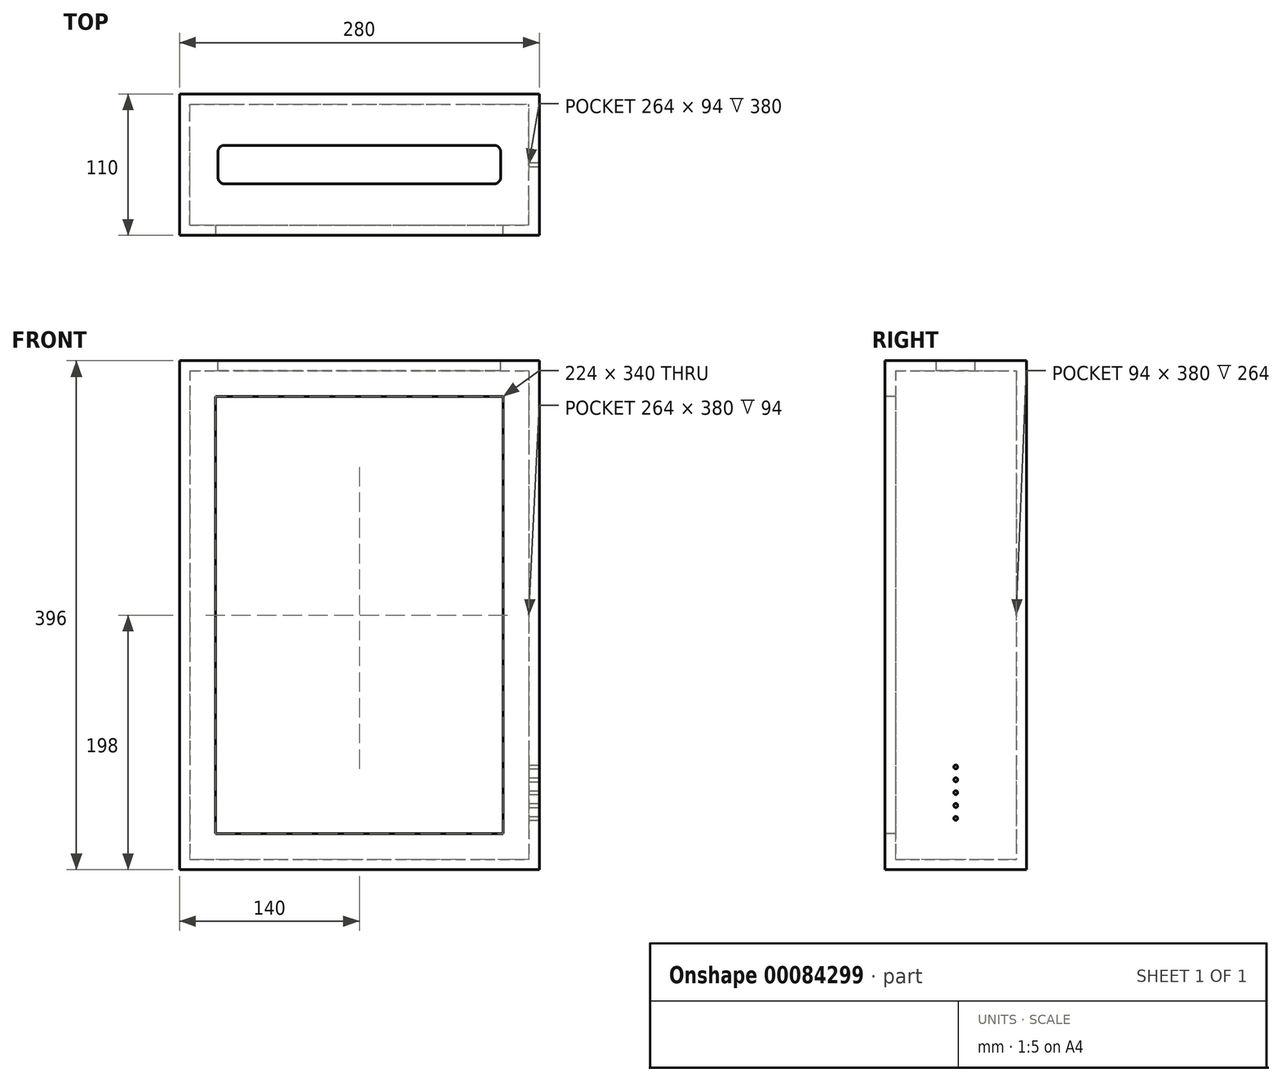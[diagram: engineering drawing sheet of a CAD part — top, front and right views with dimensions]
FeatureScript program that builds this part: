
annotation { "Feature Type Name" : "Feature", "Feature Type Description" : "" }
export const myFeature = defineFeature(function(context is Context, id is Id, definition is map)
    precondition{}
    {
        {
            var Q0;
            Q0=qCreatedBy(makeId("Top.planeOp"),FACE);
            var sketch = newSketch(context, id + "F0", { "sketchPlane" : qUnion([Q0])});
            skLineSegment(sketch, "E0.bottom", {"start": v(-140, 55) * mm, "end": v(140, 55) * mm});
            skLineSegment(sketch, "E0.top", {"start": v(-140, -55) * mm, "end": v(140, -55) * mm});
            skLineSegment(sketch, "E0.left", {"start": v(-140, 55) * mm, "end": v(-140, -55) * mm});
            skLineSegment(sketch, "E0.right", {"start": v(140, 55) * mm, "end": v(140, -55) * mm});
            skPoint(sketch, "E0.middle", {"position": v(0, 0) * mm});
            skSolve(sketch);
        }
        {
            var Q0;
            Q0=makeQuery(id+"F0.imprint","IMPRINT",FACE,{"disambiguationData":[TD([[makeQuery(id+"F0.imprint","IMPRINT",EDGE,{"derivedFrom":sQuery(id+"F0.wireOp",EDGE,"E0.bottom")}),-1.0]])]});
            extrude(context, id + "F1", {"entities" : qUnion([Q0]), "depth" : 8 * mm});
        }
        {
            var Q0;
            Q0=makeQuery(id+"F1.opExtrude","CAP_FACE",FACE,{"disambiguationData":[OSD([sQuery(id+"F0.wireOp",EDGE,"E0.bottom"),sQuery(id+"F0.wireOp",EDGE,"E0.top"),sQuery(id+"F0.wireOp",EDGE,"E0.left"),sQuery(id+"F0.wireOp",EDGE,"E0.right")])],"isStart":false});
            var sketch = newSketch(context, id + "F2", { "sketchPlane" : qUnion([Q0])});
            skLineSegment(sketch, "E1.bottom", {"start": v(-140, -55) * mm, "end": v(140, -55) * mm});
            skLineSegment(sketch, "E1.top", {"start": v(-140, 55) * mm, "end": v(140, 55) * mm});
            skLineSegment(sketch, "E1.left", {"start": v(-140, -55) * mm, "end": v(-140, 55) * mm});
            skLineSegment(sketch, "E1.right", {"start": v(140, -55) * mm, "end": v(140, 55) * mm});
            skPoint(sketch, "E1.middle", {"position": v(0, 0) * mm});
            skLineSegment(sketch, "E2.bottom", {"start": v(-132, -47) * mm, "end": v(132, -47) * mm});
            skLineSegment(sketch, "E2.top", {"start": v(-132, 47) * mm, "end": v(132, 47) * mm});
            skLineSegment(sketch, "E2.left", {"start": v(-132, -47) * mm, "end": v(-132, 47) * mm});
            skLineSegment(sketch, "E2.right", {"start": v(132, -47) * mm, "end": v(132, 47) * mm});
            skSolve(sketch);
        }
        {
            var Q0;
            Q0=makeQuery(id+"F2.imprint","IMPRINT",FACE,{"disambiguationData":[TD([[makeQuery(id+"F2.imprint","IMPRINT",EDGE,{"derivedFrom":sQuery(id+"F2.wireOp",EDGE,"E1.bottom")}),1.0]])]});
            extrude(context, id + "F3", {"entities" : qUnion([Q0]), "operationType" : NewBodyOperationType.ADD, "depth" : 20 * mm});
        }
        {
            var Q0;
            Q0=makeQuery(id+"F3.opExtrude","CAP_FACE",FACE,{"disambiguationData":[OSD([sQuery(id+"F2.wireOp",EDGE,"E1.bottom"),sQuery(id+"F2.wireOp",EDGE,"E1.top"),sQuery(id+"F2.wireOp",EDGE,"E1.left"),sQuery(id+"F2.wireOp",EDGE,"E1.right"),sQuery(id+"F2.wireOp",EDGE,"E2.bottom"),sQuery(id+"F2.wireOp",EDGE,"E2.top"),sQuery(id+"F2.wireOp",EDGE,"E2.left"),sQuery(id+"F2.wireOp",EDGE,"E2.right")])],"isStart":false});
            var sketch = newSketch(context, id + "F4", { "sketchPlane" : qUnion([Q0])});
            skLineSegment(sketch, "E3", {"start": v(-132, 47) * mm, "end": v(-132, -47) * mm});
            skLineSegment(sketch, "E4", {"start": v(-132, -47) * mm, "end": v(-112, -47) * mm});
            skLineSegment(sketch, "E5", {"start": v(-112, -47) * mm, "end": v(-112, -55) * mm});
            skLineSegment(sketch, "E6", {"start": v(-112, -55) * mm, "end": v(-140, -55) * mm});
            skLineSegment(sketch, "E7", {"start": v(-140, -55) * mm, "end": v(-140, 55) * mm});
            skLineSegment(sketch, "E8", {"start": v(-140, 55) * mm, "end": v(140, 55) * mm});
            skLineSegment(sketch, "E9", {"start": v(140, 55) * mm, "end": v(140, -55) * mm});
            skLineSegment(sketch, "E10", {"start": v(140, -55) * mm, "end": v(112, -55) * mm});
            skLineSegment(sketch, "E11", {"start": v(112, -55) * mm, "end": v(112, -47) * mm});
            skLineSegment(sketch, "E12", {"start": v(112, -47) * mm, "end": v(132, -47) * mm});
            skLineSegment(sketch, "E13", {"start": v(132, -47) * mm, "end": v(132, 47) * mm});
            skLineSegment(sketch, "E14", {"start": v(132, 47) * mm, "end": v(-132, 47) * mm});
            skSolve(sketch);
        }
        {
            var Q0;
            Q0=makeQuery(id+"F4.imprint","IMPRINT",FACE,{"disambiguationData":[TD([[makeQuery(id+"F4.imprint","IMPRINT",EDGE,{"derivedFrom":sQuery(id+"F4.wireOp",EDGE,"E3")}),1.0]])]});
            extrude(context, id + "F5", {"entities" : qUnion([Q0]), "operationType" : NewBodyOperationType.ADD, "depth" : 340 * mm});
        }
        {
            var Q0;
            Q0=makeQuery(id+"F5.opExtrude","CAP_FACE",FACE,{"disambiguationData":[OSD([sQuery(id+"F4.wireOp",EDGE,"E3"),sQuery(id+"F4.wireOp",EDGE,"E4"),sQuery(id+"F4.wireOp",EDGE,"E5"),sQuery(id+"F4.wireOp",EDGE,"E6"),sQuery(id+"F4.wireOp",EDGE,"E7"),sQuery(id+"F4.wireOp",EDGE,"E8"),sQuery(id+"F4.wireOp",EDGE,"E9"),sQuery(id+"F4.wireOp",EDGE,"E10"),sQuery(id+"F4.wireOp",EDGE,"E11"),sQuery(id+"F4.wireOp",EDGE,"E12"),sQuery(id+"F4.wireOp",EDGE,"E13"),sQuery(id+"F4.wireOp",EDGE,"E14")])],"isStart":false});
            var sketch = newSketch(context, id + "F6", { "sketchPlane" : qUnion([Q0])});
            skLineSegment(sketch, "E15.bottom", {"start": v(-132, -47) * mm, "end": v(132, -47) * mm});
            skLineSegment(sketch, "E15.top", {"start": v(-132, 47) * mm, "end": v(132, 47) * mm});
            skLineSegment(sketch, "E15.left", {"start": v(-132, -47) * mm, "end": v(-132, 47) * mm});
            skLineSegment(sketch, "E15.right", {"start": v(132, -47) * mm, "end": v(132, 47) * mm});
            skPoint(sketch, "E15.middle", {"position": v(0, 0) * mm});
            skLineSegment(sketch, "E16.bottom", {"start": v(-140, -55) * mm, "end": v(140, -55) * mm});
            skLineSegment(sketch, "E16.top", {"start": v(-140, 55) * mm, "end": v(140, 55) * mm});
            skLineSegment(sketch, "E16.left", {"start": v(-140, -55) * mm, "end": v(-140, 55) * mm});
            skLineSegment(sketch, "E16.right", {"start": v(140, -55) * mm, "end": v(140, 55) * mm});
            skSolve(sketch);
        }
        {
            var Q0;
            {var subQ1=makeQuery(id+"F5.opExtrude","CAP_EDGE",EDGE,{"disambiguationData":[OSD([sQuery(id+"F4.wireOp",EDGE,"E5")])],"isStart":false});Q0=makeQuery(id+"F6.imprint","IMPRINT",FACE,{"disambiguationData":[TD([[makeQuery(id+"F6.imprint","IMPRINT",EDGE,{"derivedFrom":subQ1}),1.0]])]});}
            var Q1;
            Q1=makeQuery(id+"F6.imprint","IMPRINT",FACE,{"disambiguationData":[TD([[makeQuery(id+"F6.imprint","IMPRINT",EDGE,{"derivedFrom":sQuery(id+"F6.wireOp",EDGE,"E15.top")}),1.0]])]});
            var Q2;
            Q2 = qSketchRegion(id + "F8", true);
            extrude(context, id + "F7", {"entities" : qUnion([Q0, Q1, Q2]), "operationType" : NewBodyOperationType.ADD, "depth" : 20 * mm, "offsetDistance" : 25 * mm});
        }
        {
            var Q0;
            Q0=makeQuery(id+"F7.opExtrude","CAP_FACE",FACE,{"disambiguationData":[OSD([sQuery(id+"F6.wireOp",EDGE,"E15.bottom"),sQuery(id+"F6.wireOp",EDGE,"E15.top"),sQuery(id+"F6.wireOp",EDGE,"E15.left"),sQuery(id+"F6.wireOp",EDGE,"E15.right"),sQuery(id+"F6.wireOp",EDGE,"E16.bottom"),sQuery(id+"F6.wireOp",EDGE,"E16.top"),sQuery(id+"F6.wireOp",EDGE,"E16.left"),sQuery(id+"F6.wireOp",EDGE,"E16.right")])],"isStart":false});
            var sketch = newSketch(context, id + "F8", { "sketchPlane" : qUnion([Q0])});
            skLineSegment(sketch, "E17.bottom", {"start": v(-140, -55) * mm, "end": v(140, -55) * mm});
            skLineSegment(sketch, "E17.top", {"start": v(-140, 55) * mm, "end": v(140, 55) * mm});
            skLineSegment(sketch, "E17.left", {"start": v(-140, -55) * mm, "end": v(-140, 55) * mm});
            skLineSegment(sketch, "E17.right", {"start": v(140, -55) * mm, "end": v(140, 55) * mm});
            skPoint(sketch, "E17.middle", {"position": v(0, 0) * mm});
            skSolve(sketch);
        }
        {
            var Q0;
            Q0=makeQuery(id+"F8.imprint","IMPRINT",FACE,{"disambiguationData":[TD([[makeQuery(id+"F8.imprint","IMPRINT",EDGE,{"derivedFrom":sQuery(id+"F8.wireOp",EDGE,"E17.bottom")}),1.0]])]});
            var Q1;
            Q1=makeQuery(id+"F8.imprint","IMPRINT",FACE,{"disambiguationData":[TD([[makeQuery(id+"F8.imprint","IMPRINT",EDGE,{"derivedFrom":makeQuery(id+"F7.opExtrude","CAP_EDGE",EDGE,{"disambiguationData":[OSD([sQuery(id+"F6.wireOp",EDGE,"E15.bottom")])],"isStart":false})}),1.0]])]});
            extrude(context, id + "F9", {"entities" : qUnion([Q0, Q1]), "operationType" : NewBodyOperationType.ADD, "depth" : 8 * mm, "offsetDistance" : 25 * mm});
        }
        {
            var Q0;
            Q0=makeQuery(id+"F9.boolean.opBoolean","MERGE",FACE,{"derivedFrom":[makeQuery(id+"F7.boolean.opBoolean","MERGE",FACE,{"derivedFrom":[makeQuery(id+"F5.boolean.opBoolean","MERGE",FACE,{"derivedFrom":[makeQuery(id+"F3.boolean.opBoolean","MERGE",FACE,{"derivedFrom":[makeQuery(id+"F1.opExtrude","SWEPT_FACE",FACE,{"disambiguationData":[OSD([sQuery(id+"F0.wireOp",EDGE,"E0.right")])]}),makeQuery(id+"F3.opExtrude","SWEPT_FACE",FACE,{"disambiguationData":[OSD([sQuery(id+"F2.wireOp",EDGE,"E1.right")])]})]}),makeQuery(id+"F5.opExtrude","SWEPT_FACE",FACE,{"disambiguationData":[OSD([sQuery(id+"F4.wireOp",EDGE,"E9")])]})]}),makeQuery(id+"F7.opExtrude","SWEPT_FACE",FACE,{"disambiguationData":[OSD([sQuery(id+"F6.wireOp",EDGE,"E16.right")])]})]}),makeQuery(id+"F9.opExtrude","SWEPT_FACE",FACE,{"disambiguationData":[OSD([sQuery(id+"F8.wireOp",EDGE,"E17.right")])]})]});
            var sketch = newSketch(context, id + "F10", { "sketchPlane" : qUnion([Q0])});
            skLineSegment(sketch, "E18", {"start": v(0, 0) * mm, "end": v(0, 396) * mm, "construction": true});
            skCircle(sketch, "E19", {"center": v(0, 40) * mm, "radius": 1.55 * mm});
            skCircle(sketch, "E20", {"center": v(0, 50) * mm, "radius": 1.55 * mm});
            skCircle(sketch, "E21", {"center": v(0, 60) * mm, "radius": 1.55 * mm});
            skCircle(sketch, "E22", {"center": v(0, 70) * mm, "radius": 1.55 * mm});
            skCircle(sketch, "E23", {"center": v(0, 80) * mm, "radius": 1.55 * mm});
            skSolve(sketch);
        }
        {
            var Q0;
            Q0=makeQuery(id+"F10.imprint","IMPRINT",FACE,{"disambiguationData":[TD([[makeQuery(id+"F10.imprint","IMPRINT",EDGE,{"derivedFrom":sQuery(id+"F10.wireOp",EDGE,"E23")}),1.0]])]});
            var Q1;
            Q1=makeQuery(id+"F10.imprint","IMPRINT",FACE,{"disambiguationData":[TD([[makeQuery(id+"F10.imprint","IMPRINT",EDGE,{"derivedFrom":sQuery(id+"F10.wireOp",EDGE,"E22")}),1.0]])]});
            var Q2;
            Q2=makeQuery(id+"F10.imprint","IMPRINT",FACE,{"disambiguationData":[TD([[makeQuery(id+"F10.imprint","IMPRINT",EDGE,{"derivedFrom":sQuery(id+"F10.wireOp",EDGE,"E20")}),1.0]])]});
            var Q3;
            Q3=makeQuery(id+"F10.imprint","IMPRINT",FACE,{"disambiguationData":[TD([[makeQuery(id+"F10.imprint","IMPRINT",EDGE,{"derivedFrom":sQuery(id+"F10.wireOp",EDGE,"E19")}),1.0]])]});
            var Q4;
            Q4=makeQuery(id+"F10.imprint","IMPRINT",FACE,{"disambiguationData":[TD([[makeQuery(id+"F10.imprint","IMPRINT",EDGE,{"derivedFrom":sQuery(id+"F10.wireOp",EDGE,"E21")}),1.0]])]});
            extrude(context, id + "F11", {"entities" : qUnion([Q0, Q1, Q2, Q3, Q4]), "operationType" : NewBodyOperationType.REMOVE, "endBound" : BoundingType.UP_TO_NEXT, "oppositeDirection" : true, "depth" : 25 * mm, "offsetDistance" : 25 * mm});
        }
        {
            var Q0;
            Q0=makeQuery(id+"F9.opExtrude","CAP_FACE",FACE,{"disambiguationData":[OSD([sQuery(id+"F8.wireOp",EDGE,"E17.bottom"),sQuery(id+"F8.wireOp",EDGE,"E17.top"),sQuery(id+"F8.wireOp",EDGE,"E17.left"),sQuery(id+"F8.wireOp",EDGE,"E17.right")])],"isStart":false});
            var sketch = newSketch(context, id + "F12", { "sketchPlane" : qUnion([Q0])});
            skLineSegment(sketch, "E24.bottom", {"start": v(-110, -15) * mm, "end": v(110, -15) * mm});
            skLineSegment(sketch, "E24.top", {"start": v(-110, 15) * mm, "end": v(110, 15) * mm});
            skLineSegment(sketch, "E24.left", {"start": v(-110, -15) * mm, "end": v(-110, 15) * mm});
            skLineSegment(sketch, "E24.right", {"start": v(110, -15) * mm, "end": v(110, 15) * mm});
            skPoint(sketch, "E24.middle", {"position": v(0, 0) * mm});
            skSolve(sketch);
        }
        {
            var Q0;
            Q0=makeQuery(id+"F12.imprint","IMPRINT",FACE,{"disambiguationData":[TD([[makeQuery(id+"F12.imprint","IMPRINT",EDGE,{"derivedFrom":sQuery(id+"F12.wireOp",EDGE,"E24.bottom")}),1.0]])]});
            extrude(context, id + "F13", {"entities" : qUnion([Q0]), "operationType" : NewBodyOperationType.REMOVE, "endBound" : BoundingType.UP_TO_NEXT, "oppositeDirection" : true, "depth" : 25 * mm, "offsetDistance" : 25 * mm});
        }
        {
            var Q0;
            Q0=makeQuery(id+"F13.boolean.opBoolean","COPY",EDGE,{"derivedFrom":makeQuery(id+"F13.opExtrude","SWEPT_EDGE",EDGE,{"disambiguationData":[OSD([sQuery(id+"F12.wireOp",EDGE,"E24.top"),sQuery(id+"F12.wireOp",EDGE,"E24.left")])]})});
            var Q1;
            Q1=makeQuery(id+"F13.boolean.opBoolean","COPY",EDGE,{"derivedFrom":makeQuery(id+"F13.opExtrude","SWEPT_EDGE",EDGE,{"disambiguationData":[OSD([sQuery(id+"F12.wireOp",EDGE,"E24.bottom"),sQuery(id+"F12.wireOp",EDGE,"E24.left")])]})});
            var Q2;
            Q2=makeQuery(id+"F13.boolean.opBoolean","COPY",EDGE,{"derivedFrom":makeQuery(id+"F13.opExtrude","SWEPT_EDGE",EDGE,{"disambiguationData":[OSD([sQuery(id+"F12.wireOp",EDGE,"E24.bottom"),sQuery(id+"F12.wireOp",EDGE,"E24.right")])]})});
            var Q3;
            Q3=makeQuery(id+"F13.boolean.opBoolean","COPY",EDGE,{"derivedFrom":makeQuery(id+"F13.opExtrude","SWEPT_EDGE",EDGE,{"disambiguationData":[OSD([sQuery(id+"F12.wireOp",EDGE,"E24.top"),sQuery(id+"F12.wireOp",EDGE,"E24.right")])]})});
            fillet(context, id + "F14", {"entities" : qUnion([Q0, Q1, Q2, Q3]), "radius" : 5 * mm, "tangentPropagation" : true, "allowEdgeOverflow" : false});
        }
    });
